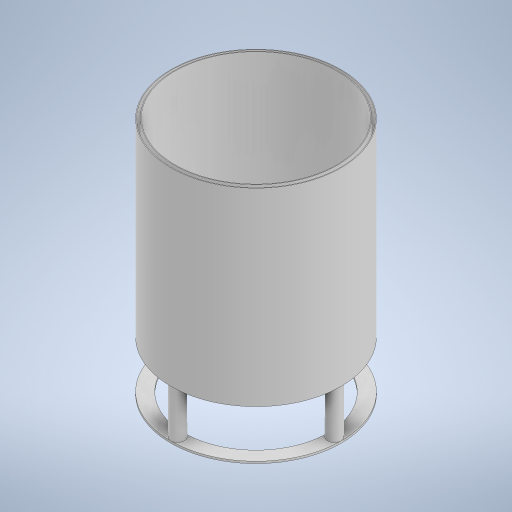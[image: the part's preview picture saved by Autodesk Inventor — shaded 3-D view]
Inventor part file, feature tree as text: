
AUTODESK INVENTOR PART (.ipt)
format: ipt  version: 2024 (Build 280153000, 153)  size: 307,712 bytes
history: native  units: mm
features: sketch x8, extrude x7, pattern_circular x1
ambient origin geometry x8: Origin, YZ Plane, XZ Plane, XY Plane, X Axis, Y Axis, Z Axis, Center Point
bodies: Solid1 (feature_tree)
feature tree (16):
  extrude  "Extrusion1"  Depth=252.0mm
  extrude  "Extrusion3"  Depth=1.0mm TaperAngle=0.0deg
  extrude  "Extrusion8"  Depth=30.0mm TaperAngle=0.0deg
  sketch  "Sketch9"  dims[d21=70.0mm d22=0.0mm d23=40.0mm d24=360.0deg d28=240.0mm]
  extrude  "Extrusion9"  Depth=40.0mm TaperAngle=360.0deg
  pattern_circular  "Circular Pattern1"  Count=24  [1 undecoded]
  extrude  "Extrusion12"  Depth=252.0mm
  extrude  "Extrusion14"  Depth=280.0mm
  extrude  "Extrusion15"  Depth=252.04971mm
  sketch  "Sketch1"  dims[d0=250.0mm d1=252.0mm]
  sketch  "Sketch3"  dims[d2=280.0mm d3=0.0mm d6=1.0mm d7=0.0mm]
  sketch  "Sketch8"  dims[d18=120.0mm d19=30.0mm d20=0.0mm]
  sketch  "Sketch10"  dims[d29=242.0mm d32=252.0mm]
  sketch  "Sketch12"  dims[d33=280.0mm d34=0.0mm d35=20.0mm]
  sketch  "Sketch13"  dims[d38=212.0mm d39=252.04971mm]
  sketch  "Sketch14"  dims[d40=3.0mm d41=0.0mm d42=18.0mm d43=118.0mm d44=1.0mm d45=0.0mm d4=0.5mm d5=0.872665mm]
note: 1 required parameter value undecoded (feature->parameter linkage not recoverable at this tier; creation-order binding heuristic only, values carry confidence <= 0.55)
